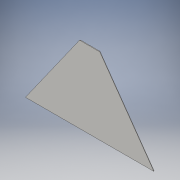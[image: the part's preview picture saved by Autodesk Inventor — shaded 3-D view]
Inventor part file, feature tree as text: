
AUTODESK INVENTOR PART (.ipt)
format: ipt  version: 2016 (Build 200138000, 138)  size: 98,816 bytes
history: native  units: in
note: dims shown in document units (in); Inventor stores cm internally (conversion verified against a paired STEP export)
features: chamfer x2, extrude x1, sketch x1
ambient origin geometry x8: Origin, YZ Plane, XZ Plane, XY Plane, X Axis, Y Axis, Z Axis, Center Point
bodies: Solid1 (feature_tree)
feature tree (4):
  extrude  "Extrusion1"  Depth=0.0197in
  chamfer  "Chamfer2"  Distance=0.5906in
  chamfer  "Chamfer3"  Distance=2.227in
  sketch  "Sketch1"  dims[d0=2.7276in d1=3.7402in d2=0.5906in d3=2.227in d4=2.7276in d5=0.0197in d6=0.0in d10=0.0197in d11=0.125in d12=30.0deg d13=0.0197in d14=0.125in d15=30.0deg]
